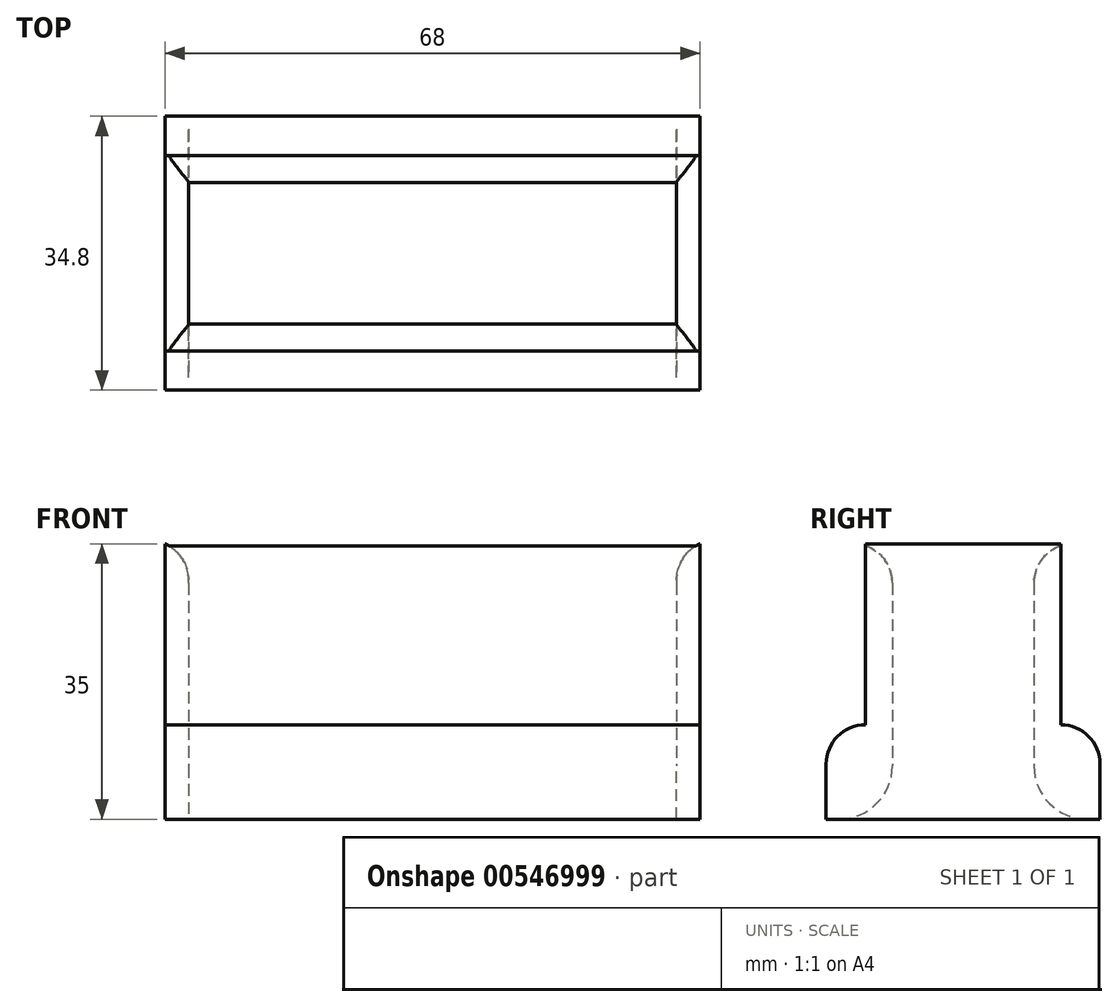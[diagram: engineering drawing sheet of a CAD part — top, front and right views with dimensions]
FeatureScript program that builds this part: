
annotation { "Feature Type Name" : "Feature", "Feature Type Description" : "" }
export const myFeature = defineFeature(function(context is Context, id is Id, definition is map)
    precondition{}
    {
        {
            var Q0;
            Q0=qCreatedBy(makeId("Top.planeOp"),FACE);
            var sketch = newSketch(context, id + "F0", { "sketchPlane" : qUnion([Q0])});
            skLineSegment(sketch, "E0.bottom", {"start": v(31, -9) * mm, "end": v(-31, -9) * mm});
            skLineSegment(sketch, "E0.top", {"start": v(31, 9) * mm, "end": v(-31, 9) * mm});
            skLineSegment(sketch, "E0.left", {"start": v(31, -9) * mm, "end": v(31, 9) * mm});
            skLineSegment(sketch, "E0.right", {"start": v(-31, -9) * mm, "end": v(-31, 9) * mm});
            skPoint(sketch, "E0.middle", {"position": v(0, 0) * mm});
            skLineSegment(sketch, "E1.bottom", {"start": v(34, -12.4) * mm, "end": v(-34, -12.4) * mm});
            skLineSegment(sketch, "E1.top", {"start": v(34, 12.4) * mm, "end": v(-34, 12.4) * mm});
            skLineSegment(sketch, "E1.left", {"start": v(34, -12.4) * mm, "end": v(34, 12.4) * mm});
            skLineSegment(sketch, "E1.right", {"start": v(-34, -12.4) * mm, "end": v(-34, 12.4) * mm});
            skLineSegment(sketch, "E2.bottom", {"start": v(34, -17.4) * mm, "end": v(-34, -17.4) * mm});
            skLineSegment(sketch, "E2.top", {"start": v(34, 17.4) * mm, "end": v(-34, 17.4) * mm});
            skLineSegment(sketch, "E2.left", {"start": v(34, -17.4) * mm, "end": v(34, 17.4) * mm});
            skLineSegment(sketch, "E2.right", {"start": v(-34, -17.4) * mm, "end": v(-34, 17.4) * mm});
            skSolve(sketch);
        }
        {
            var Q0;
            Q0=makeQuery(id+"F0.imprint","IMPRINT",FACE,{"disambiguationData":[TD([[makeQuery(id+"F0.imprint","IMPRINT",EDGE,{"derivedFrom":sQuery(id+"F0.wireOp",EDGE,"E0.bottom")}),1.0]])]});
            extrude(context, id + "F1", {"entities" : qUnion([Q0]), "depth" : 35 * mm, "offsetDistance" : 25 * mm});
        }
        {
            var Q0;
            {var subQ0=sQuery(id+"F0.wireOp",EDGE,"E1.top");Q0=makeQuery(id+"F0.imprint","IMPRINT",FACE,{"disambiguationData":[TD([[makeQuery(id+"F0.imprint","IMPRINT",EDGE,{"derivedFrom":subQ0}),-1.0]])]});}
            var Q1;
            {var subQ0=sQuery(id+"F0.wireOp",EDGE,"E1.bottom");Q1=makeQuery(id+"F0.imprint","IMPRINT",FACE,{"disambiguationData":[TD([[makeQuery(id+"F0.imprint","IMPRINT",EDGE,{"derivedFrom":subQ0}),1.0]])]});}
            extrude(context, id + "F2", {"entities" : qUnion([Q0, Q1]), "operationType" : NewBodyOperationType.ADD, "depth" : 12 * mm, "offsetDistance" : 25 * mm});
        }
        {
            var Q0;
            Q0=makeQuery(id+"F1.opExtrude","CAP_EDGE",EDGE,{"disambiguationData":[OSD([sQuery(id+"F0.wireOp",EDGE,"E0.top")])],"isStart":true});
            fillet(context, id + "F3", {"entities" : qUnion([Q0]), "radius" : 6.76 * mm, "tangentPropagation" : true, "allowEdgeOverflow" : false});
        }
        {
            var Q0;
            Q0=makeQuery(id+"F1.opExtrude","CAP_EDGE",EDGE,{"disambiguationData":[OSD([sQuery(id+"F0.wireOp",EDGE,"E0.bottom")])],"isStart":true});
            fillet(context, id + "F4", {"entities" : qUnion([Q0]), "radius" : 6.76 * mm, "tangentPropagation" : true, "allowEdgeOverflow" : false});
        }
        {
            var Q0;
            Q0=makeQuery(id+"F2.opExtrude","CAP_EDGE",EDGE,{"disambiguationData":[OSD([sQuery(id+"F0.wireOp",EDGE,"E2.top")])],"isStart":false});
            fillet(context, id + "F5", {"entities" : qUnion([Q0]), "radius" : 5 * mm, "tangentPropagation" : true, "allowEdgeOverflow" : false});
        }
        {
            var Q0;
            Q0=makeQuery(id+"F2.opExtrude","CAP_EDGE",EDGE,{"disambiguationData":[OSD([sQuery(id+"F0.wireOp",EDGE,"E2.bottom")])],"isStart":false});
            fillet(context, id + "F6", {"entities" : qUnion([Q0]), "radius" : 5 * mm, "tangentPropagation" : true, "allowEdgeOverflow" : false});
        }
        {
            var Q0;
            Q0=makeQuery(id+"F1.opExtrude","CAP_EDGE",EDGE,{"disambiguationData":[OSD([sQuery(id+"F0.wireOp",EDGE,"E0.top")])],"isStart":false});
            fillet(context, id + "F7", {"entities" : qUnion([Q0]), "radius" : 5 * mm, "tangentPropagation" : true, "allowEdgeOverflow" : false});
        }
        {
            var Q0;
            Q0=makeQuery(id+"F1.opExtrude","CAP_EDGE",EDGE,{"disambiguationData":[OSD([sQuery(id+"F0.wireOp",EDGE,"E0.bottom")])],"isStart":false});
            fillet(context, id + "F8", {"entities" : qUnion([Q0]), "radius" : 5 * mm, "tangentPropagation" : true, "allowEdgeOverflow" : false});
        }
        {
            var Q0;
            Q0=makeQuery(id+"F1.opExtrude","CAP_EDGE",EDGE,{"disambiguationData":[OSD([sQuery(id+"F0.wireOp",EDGE,"E0.right")])],"isStart":false});
            fillet(context, id + "F9", {"entities" : qUnion([Q0]), "radius" : 5 * mm, "tangentPropagation" : true, "allowEdgeOverflow" : false});
        }
        {
            var Q0;
            Q0=makeQuery(id+"F1.opExtrude","CAP_EDGE",EDGE,{"disambiguationData":[OSD([sQuery(id+"F0.wireOp",EDGE,"E0.left")])],"isStart":false});
            fillet(context, id + "F10", {"entities" : qUnion([Q0]), "radius" : 5 * mm, "tangentPropagation" : true, "allowEdgeOverflow" : false});
        }
    });
